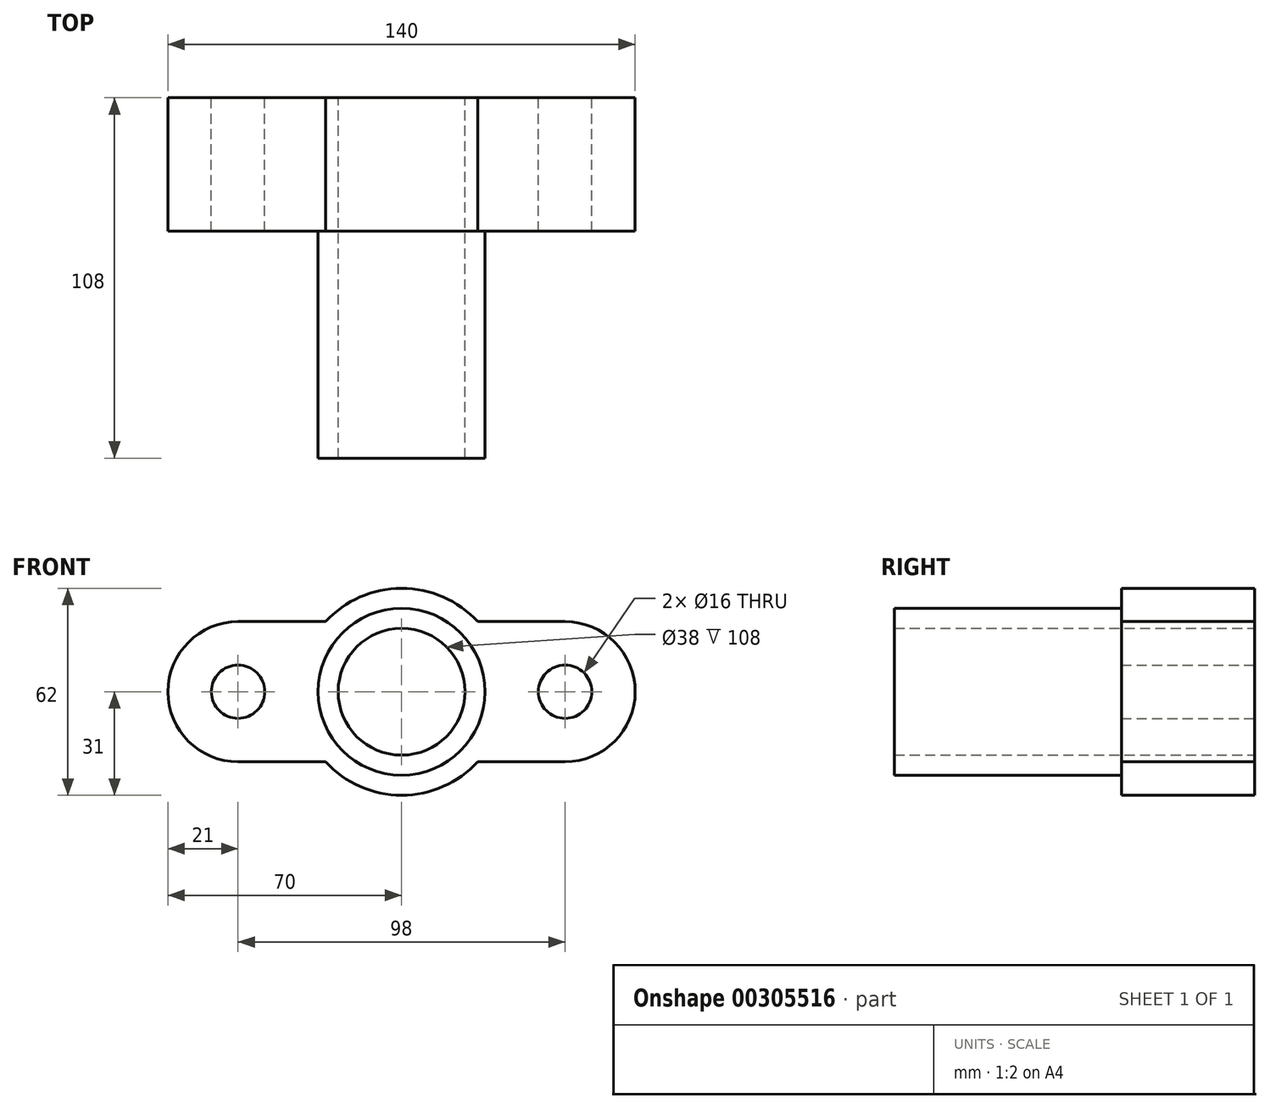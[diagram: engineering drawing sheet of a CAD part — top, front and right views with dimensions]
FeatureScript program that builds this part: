
annotation { "Feature Type Name" : "Feature", "Feature Type Description" : "" }
export const myFeature = defineFeature(function(context is Context, id is Id, definition is map)
    precondition{}
    {
        {
            var Q0;
            Q0=qCreatedBy(makeId("Front.planeOp"),FACE);
            var sketch = newSketch(context, id + "F0", { "sketchPlane" : qUnion([Q0])});
            skArc(sketch, "E0", {"start": v(-22.8, -21) * mm, "mid": v(0, -31) * mm, "end": v(22.8, -21) * mm});
            skCircle(sketch, "E1", {"center": v(0, 0) * mm, "radius": 25 * mm});
            skCircle(sketch, "E2", {"center": v(0, 0) * mm, "radius": 19 * mm});
            skLineSegment(sketch, "E3", {"start": v(0, 54.15) * mm, "end": v(0, -62.09) * mm, "construction": true});
            skLineSegment(sketch, "E4.0", {"start": v(-49, 54.15) * mm, "end": v(-49, -62.09) * mm, "construction": true});
            skLineSegment(sketch, "E5.0", {"start": v(49, 54.15) * mm, "end": v(49, -62.09) * mm, "construction": true});
            skCircle(sketch, "E6", {"center": v(-49, 0) * mm, "radius": 8 * mm});
            skCircle(sketch, "E7", {"center": v(49, 0) * mm, "radius": 8 * mm});
            skCircle(sketch, "E8", {"center": v(-49, 0) * mm, "radius": 21 * mm});
            skCircle(sketch, "E9", {"center": v(49, 0) * mm, "radius": 21 * mm});
            skLineSegment(sketch, "E10", {"start": v(-49, 21) * mm, "end": v(-22.8, 21) * mm});
            skLineSegment(sketch, "E11", {"start": v(49, 21) * mm, "end": v(49, -21) * mm});
            skLineSegment(sketch, "E12", {"start": v(49, -21) * mm, "end": v(22.8, -21) * mm});
            skLineSegment(sketch, "E13.trimOffspring", {"start": v(22.8, 21) * mm, "end": v(49, 21) * mm});
            skLineSegment(sketch, "E14.trimOffspring", {"start": v(-22.8, -21) * mm, "end": v(-49, -21) * mm});
            skArc(sketch, "E15.trimOffspring", {"start": v(22.8, 21) * mm, "mid": v(0, 31) * mm, "end": v(-22.8, 21) * mm});
            skSolve(sketch);
        }
        {
            var Q0;
            Q0 = qSketchRegion(id + "F0", true);
            var Q1;
            Q1=makeQuery(id+"F0.imprint","IMPRINT",FACE,{"disambiguationData":[TD([[makeQuery(id+"F0.imprint","IMPRINT",EDGE,{"derivedFrom":sQuery(id+"F0.wireOp",EDGE,"E1")}),1.0]])]});
            extrude(context, id + "F1", {"entities" : qUnion([Q0, Q1]), "depth" : 40 * mm});
        }
        {
            var Q0;
            Q0=makeQuery(id+"F0.imprint","IMPRINT",FACE,{"disambiguationData":[TD([[makeQuery(id+"F0.imprint","IMPRINT",EDGE,{"derivedFrom":sQuery(id+"F0.wireOp",EDGE,"E1")}),1.0]])]});
            extrude(context, id + "F2", {"entities" : qUnion([Q0]), "operationType" : NewBodyOperationType.ADD, "depth" : 108 * mm});
        }
    });
